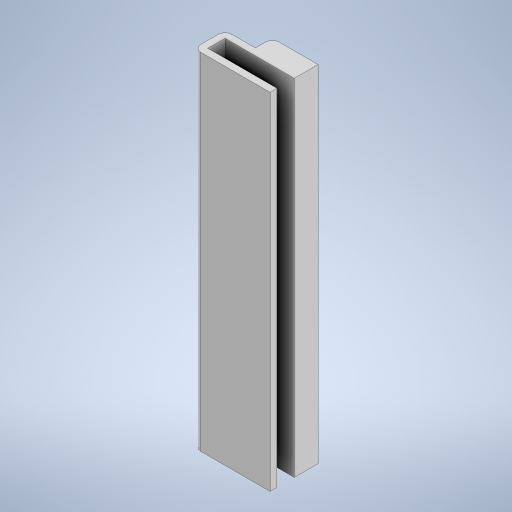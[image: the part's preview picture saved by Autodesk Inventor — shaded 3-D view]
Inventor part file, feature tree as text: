
AUTODESK INVENTOR PART (.ipt)
format: ipt  version: 2024 (Build 280153000, 153)  size: 273,408 bytes
history: native  units: in
note: dims shown in document units (in); Inventor stores cm internally (conversion verified against a paired STEP export)
features: extrude x2, sketch x2, fillet x1
ambient origin geometry x8: Origin, YZ Plane, XZ Plane, XY Plane, X Axis, Y Axis, Z Axis, Center Point
bodies: Solid1 (feature_tree)
feature tree (5):
  extrude  "Extrusion1"  Depth=0.1in
  extrude  "Extrusion3"  Depth=0.45in
  fillet  "Fillet3"  Radius=0.1in
  sketch  "Sketch1"  dims[d0=1.0in d1=0.1in]
  sketch  "Sketch4"  dims[d2=0.1in d3=0.45in d4=0.1in d5=5.0in d6=0.0in d15=0.3898in d16=0.33in d17=1.9685in d19=1.0in d20=0.3937in d22=1.0in d24=0.5in d25=0.1181in d26=0.0in d27=0.1in]
